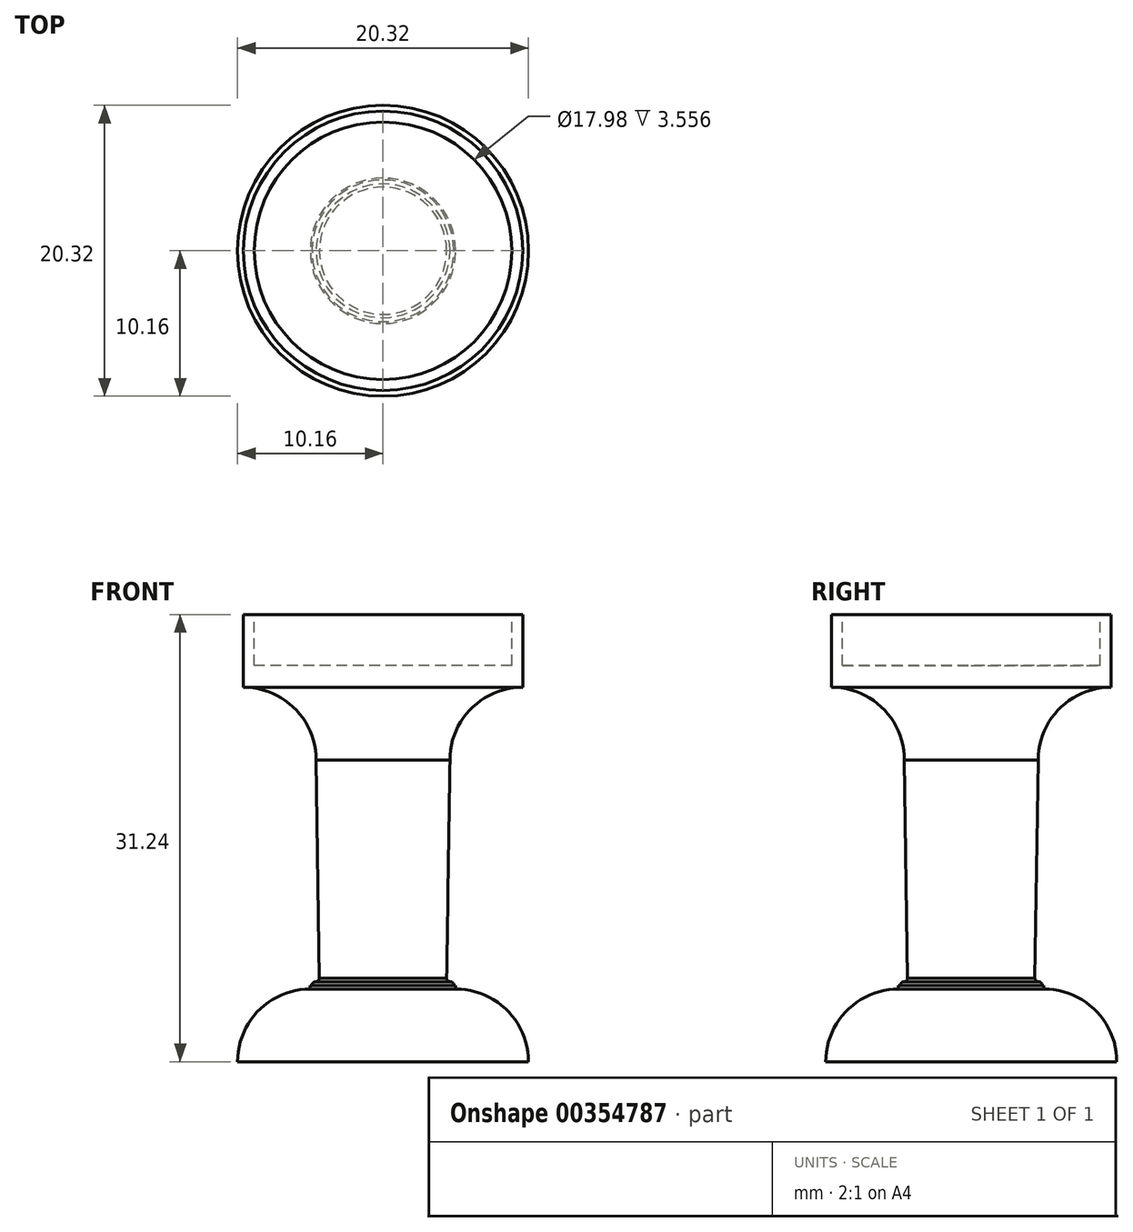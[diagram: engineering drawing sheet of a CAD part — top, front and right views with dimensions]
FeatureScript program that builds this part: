
annotation { "Feature Type Name" : "Feature", "Feature Type Description" : "" }
export const myFeature = defineFeature(function(context is Context, id is Id, definition is map)
    precondition{}
    {
        {
            var Q0;
            Q0=qCreatedBy(makeId("Front.planeOp"),FACE);
            var sketch = newSketch(context, id + "F0", { "sketchPlane" : qUnion([Q0])});
            skLineSegment(sketch, "E0", {"start": v(0, 0) * mm, "end": v(-10.16, 0) * mm});
            skLineSegment(sketch, "E1", {"start": v(-10.16, 0) * mm, "end": v(-5.08, 0) * mm, "construction": true});
            skLineSegment(sketch, "E2", {"start": v(-5.08, 0) * mm, "end": v(-5.08, 5.08) * mm, "construction": true});
            skArc(sketch, "E3", {"start": v(-10.16, 0) * mm, "mid": v(-8.67, 3.6) * mm, "end": v(-5.08, 5.08) * mm});
            skLineSegment(sketch, "E4", {"start": v(-5.08, 5.08) * mm, "end": v(-5.08, 5.33) * mm});
            skLineSegment(sketch, "E5", {"start": v(-5.08, 5.33) * mm, "end": v(-4.95, 5.33) * mm});
            skLineSegment(sketch, "E6", {"start": v(-4.95, 5.33) * mm, "end": v(-4.7, 5.33) * mm, "construction": true});
            skLineSegment(sketch, "E7", {"start": v(-4.7, 5.33) * mm, "end": v(-4.7, 5.59) * mm, "construction": true});
            skArc(sketch, "E8", {"start": v(-4.95, 5.33) * mm, "mid": v(-4.88, 5.51) * mm, "end": v(-4.7, 5.59) * mm});
            skLineSegment(sketch, "E9", {"start": v(-4.7, 5.59) * mm, "end": v(-4.7, 5.84) * mm, "construction": true});
            skLineSegment(sketch, "E10", {"start": v(-4.7, 5.84) * mm, "end": v(-4.45, 5.84) * mm, "construction": true});
            skArc(sketch, "E11", {"start": v(-4.7, 5.59) * mm, "mid": v(-4.52, 5.66) * mm, "end": v(-4.45, 5.84) * mm});
            skLineSegment(sketch, "E12", {"start": v(-4.45, 5.84) * mm, "end": v(-4.45, 21.08) * mm, "construction": true});
            skLineSegment(sketch, "E13", {"start": v(-4.45, 21.08) * mm, "end": v(-4.67, 21.08) * mm, "construction": true});
            skLineSegment(sketch, "E14", {"start": v(-4.45, 5.84) * mm, "end": v(-4.67, 21.08) * mm});
            skLineSegment(sketch, "E15", {"start": v(-4.67, 21.08) * mm, "end": v(-9.75, 21.08) * mm, "construction": true});
            skLineSegment(sketch, "E16", {"start": v(-9.75, 21.08) * mm, "end": v(-9.75, 26.16) * mm, "construction": true});
            skArc(sketch, "E17", {"start": v(-4.67, 21.08) * mm, "mid": v(-6.16, 24.67) * mm, "end": v(-9.75, 26.16) * mm});
            skLineSegment(sketch, "E18", {"start": v(-9.75, 26.16) * mm, "end": v(-9.75, 31.24) * mm});
            skLineSegment(sketch, "E19", {"start": v(-9.75, 31.24) * mm, "end": v(0, 31.24) * mm});
            skLineSegment(sketch, "E20", {"start": v(0, 31.24) * mm, "end": v(0, 0) * mm});
            skSolve(sketch);
        }
        {
            var Q0;
            Q0 = qSketchRegion(id + "F0", true);
            var Q1;
            Q1=sQuery(id+"F0.wireOp",EDGE,"E20");
            revolve(context, id + "F1", {"entities" : qUnion([Q0]), "axis" : qUnion([Q1]), "revolveType" : RevolveType.FULL});
        }
        {
            var Q0;
            Q0=makeQuery(id+"F1.opRevolve","SWEPT_FACE",FACE,{"disambiguationData":[OSD([sQuery(id+"F0.wireOp",EDGE,"E19")])]});
            var sketch = newSketch(context, id + "F2", { "sketchPlane" : qUnion([Q0])});
            skCircle(sketch, "E21", {"center": v(0, 0) * mm, "radius": 9 * mm});
            skSolve(sketch);
        }
        {
            var Q0;
            Q0 = qSketchRegion(id + "F2", true);
            extrude(context, id + "F3", {"entities" : qUnion([Q0]), "operationType" : NewBodyOperationType.REMOVE, "oppositeDirection" : true, "depth" : 3.56 * mm});
        }
        {
            var Q0;
            Q0=makeQuery(id+"F1.opRevolve","SWEPT_FACE",FACE,{"disambiguationData":[OSD([sQuery(id+"F0.wireOp",EDGE,"E19")])]});
            var sketch = newSketch(context, id + "F4", { "sketchPlane" : qUnion([Q0])});
            skLineSegment(sketch, "E22", {"start": v(-0.5, 0) * mm, "end": v(0, 0) * mm});
            skLineSegment(sketch, "E23", {"start": v(0, 0) * mm, "end": v(0, 0.5) * mm});
            skLineSegment(sketch, "E24", {"start": v(0, -0.5) * mm, "end": v(0, 0) * mm});
            skLineSegment(sketch, "E25", {"start": v(0.5, 0) * mm, "end": v(0, 0) * mm});
            skLineSegment(sketch, "E26", {"start": v(-8.06, 0.5) * mm, "end": v(7.39, 0.5) * mm});
            skLineSegment(sketch, "E27", {"start": v(-8.06, 0.5) * mm, "end": v(-8.06, -0.5) * mm});
            skLineSegment(sketch, "E28", {"start": v(-8.06, -0.5) * mm, "end": v(7.39, -0.5) * mm});
            skLineSegment(sketch, "E29", {"start": v(7.39, -0.5) * mm, "end": v(7.39, 0.5) * mm});
            skLineSegment(sketch, "E30", {"start": v(-0.5, 7) * mm, "end": v(-0.5, -7.18) * mm});
            skLineSegment(sketch, "E31", {"start": v(-0.5, -7.18) * mm, "end": v(0.5, -7.18) * mm});
            skLineSegment(sketch, "E32", {"start": v(0.5, -7.18) * mm, "end": v(0.5, 7) * mm});
            skLineSegment(sketch, "E33", {"start": v(0.5, 7) * mm, "end": v(-0.5, 7) * mm});
            skSolve(sketch);
        }
        {
            var Q0;
            Q0 = qSketchRegion(id + "F4", true);
            extrude(context, id + "F5", {"entities" : qUnion([Q0]), "operationType" : NewBodyOperationType.REMOVE, "oppositeDirection" : true, "depth" : 1.78 * mm});
        }
    });
